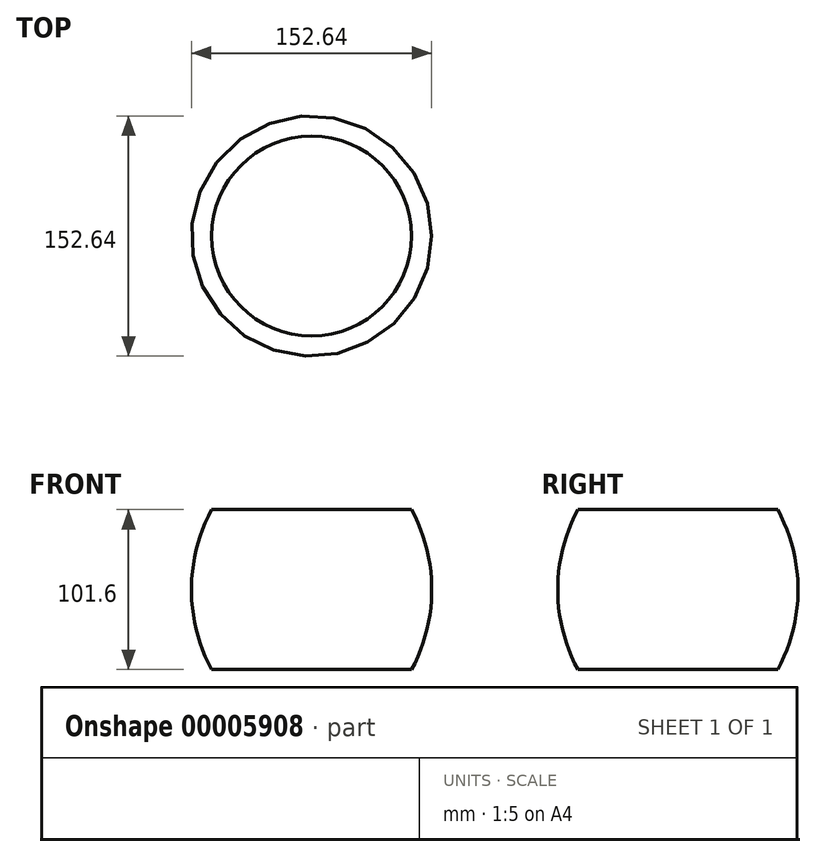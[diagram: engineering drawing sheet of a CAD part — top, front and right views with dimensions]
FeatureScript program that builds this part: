
annotation { "Feature Type Name" : "Feature", "Feature Type Description" : "" }
export const myFeature = defineFeature(function(context is Context, id is Id, definition is map)
    precondition{}
    {
        {
            var Q0;
            Q0=qCreatedBy(makeId("Front.planeOp"),FACE);
            var sketch = newSketch(context, id + "F0", { "sketchPlane" : qUnion([Q0])});
            skLineSegment(sketch, "E0", {"start": v(0, 55.81) * mm, "end": v(0, -45.79) * mm, "construction": true});
            skLineSegment(sketch, "E1", {"start": v(0, 55.81) * mm, "end": v(63.5, 55.81) * mm, "construction": true});
            skLineSegment(sketch, "E2", {"start": v(0, -45.79) * mm, "end": v(63.5, -45.79) * mm, "construction": true});
            skLineSegment(sketch, "E3", {"start": v(0, 0) * mm, "end": v(76.2, 0) * mm, "construction": true});
            skLineSegment(sketch, "E4", {"start": v(0, -45.79) * mm, "end": v(63.5, -45.79) * mm});
            skLineSegment(sketch, "E5", {"start": v(0, 55.81) * mm, "end": v(0, -45.79) * mm});
            skArc(sketch, "E6", {"start": v(63.5, -45.79) * mm, "mid": v(76.32, 5.01) * mm, "end": v(63.5, 55.81) * mm});
            skLineSegment(sketch, "E7", {"start": v(0, 55.81) * mm, "end": v(63.5, 55.81) * mm});
            skSolve(sketch);
        }
        {
            var Q0;
            Q0=makeQuery(id+"F0.imprint","IMPRINT",FACE,{"disambiguationData":[TD([[makeQuery(id+"F0.imprint","IMPRINT",EDGE,{"derivedFrom":sQuery(id+"F0.wireOp",EDGE,"E4")}),1.0]])]});
            var Q1;
            Q1=sQuery(id+"F0.wireOp",EDGE,"E5");
            revolve(context, id + "F1", {"entities" : qUnion([Q0]), "axis" : qUnion([Q1]), "revolveType" : RevolveType.FULL});
        }
    });
